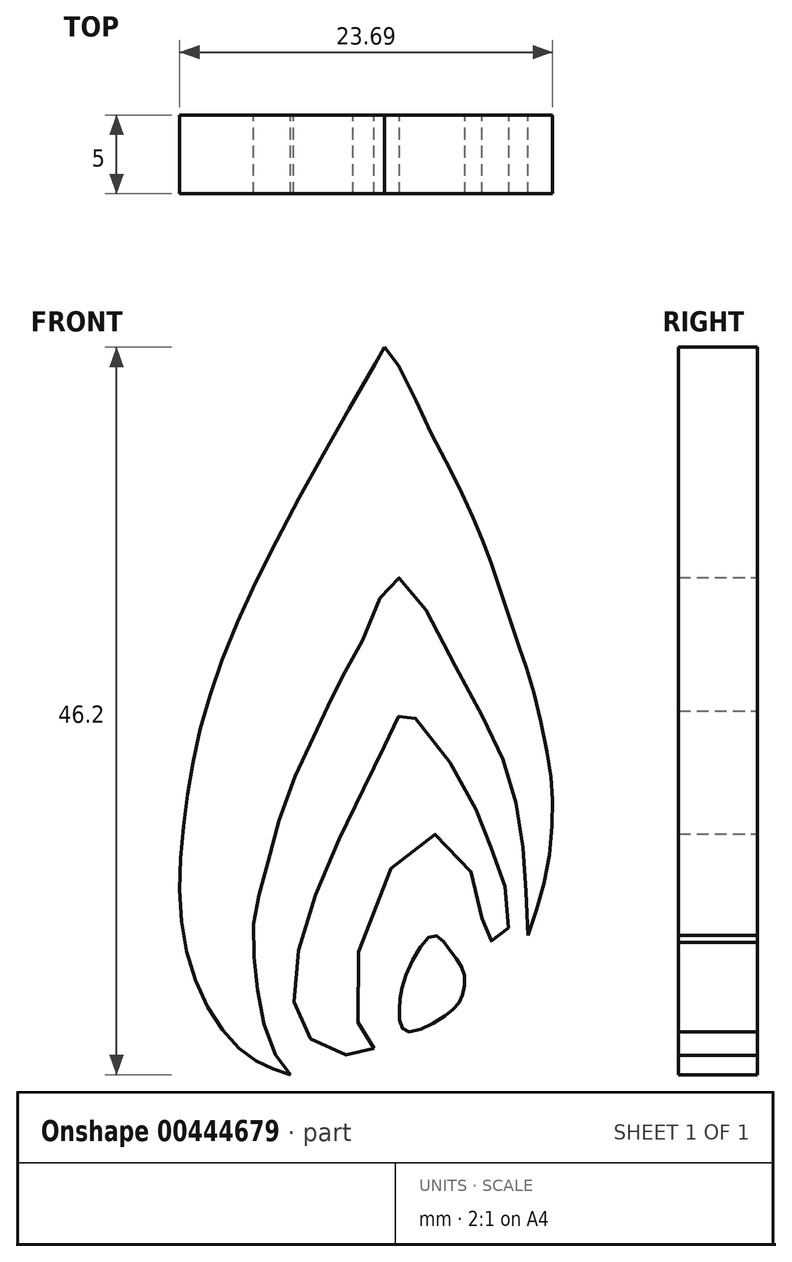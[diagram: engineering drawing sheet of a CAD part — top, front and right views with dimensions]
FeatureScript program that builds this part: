
annotation { "Feature Type Name" : "Feature", "Feature Type Description" : "" }
export const myFeature = defineFeature(function(context is Context, id is Id, definition is map)
    precondition{}
    {
        {
            var Q0;
            Q0=qCreatedBy(makeId("Front.planeOp"),FACE);
            var sketch = newSketch(context, id + "F0", { "sketchPlane" : qUnion([Q0])});
            skFitSpline(sketch, "E0", {"points": [v(-114.52, -36.4) * mm, v(-124.53, -55.47) * mm, v(-127.23, -66.27) * mm, v(-126.97, -75.26) * mm, v(-123.54, -81.14) * mm, v(-120.48, -82.6) * mm], "startDerivative": vector(-38.93, -67.33) * mm, "endDerivative": vector(25.9, -7.91) * mm});
            skFitSpline(sketch, "E1", {"points": [v(-105.42, -73.76) * mm, v(-104.24, -69.82) * mm, v(-103.84, -65.48) * mm, v(-104.14, -62.42) * mm, v(-105.23, -57.69) * mm, v(-106.21, -54.73) * mm, v(-107.79, -50) * mm, v(-108.97, -47.04) * mm, v(-110.55, -43.78) * mm, v(-111.74, -41.51) * mm, v(-114.52, -36.4) * mm, v(-115.13, -37.46) * mm], "startDerivative": vector(13.91, 39.07) * mm, "endDerivative": vector(-8.74, -32.14) * mm});
            skPoint(sketch, "E2.1.internal.orphan", {"position": v(-121.51, -80.47) * mm});
            skPoint(sketch, "E2.10.internal.orphan", {"position": v(-121.51, -70.21) * mm});
            skPoint(sketch, "E2.6.internal.orphan", {"position": v(-122.78, -75.26) * mm});
            skFitSpline(sketch, "E3", {"points": [v(-120.48, -82.6) * mm, v(-121.51, -81.26) * mm, v(-122.4, -78.31) * mm, v(-122.78, -75.26) * mm, v(-122.78, -72.47) * mm, v(-122.16, -70.02) * mm, v(-120.87, -65.33) * mm, v(-118.76, -60.6) * mm, v(-117.57, -58.04) * mm, v(-115.48, -54.06) * mm, v(-113.74, -51.03) * mm, v(-109.93, -56.83) * mm, v(-106.75, -63.2) * mm, v(-105.7, -68.57) * mm, v(-105.42, -73.76) * mm], "startDerivative": vector(-23.65, 25.1) * mm, "endDerivative": vector(2.23, -63.6) * mm});
            skFitSpline(sketch, "E4", {"points": [v(-115.18, -80.94) * mm, v(-116.41, -78.67) * mm, v(-111.88, -67.34) * mm, v(-108.43, -71.46) * mm, v(-108.17, -73.76) * mm, v(-107.1, -74.14) * mm, v(-106.68, -71.67) * mm, v(-107.81, -68.01) * mm, v(-109.67, -63.9) * mm, v(-113.17, -59.52) * mm, v(-113.58, -59.77) * mm, v(-114.61, -61.94) * mm, v(-117.29, -67.4) * mm, v(-119.97, -74.7) * mm, v(-119.76, -79.65) * mm, v(-116.98, -81.35) * mm, v(-115.18, -80.94) * mm]});
            skFitSpline(sketch, "E5", {"points": [v(-110.7, -78.88) * mm, v(-109.66, -77.8) * mm, v(-109.45, -76.2) * mm, v(-110.28, -74.81) * mm, v(-111.41, -73.76) * mm, v(-113.17, -76.36) * mm, v(-113.58, -78.62) * mm, v(-113.17, -79.86) * mm, v(-110.7, -78.88) * mm]});
            skSolve(sketch);
        }
        {
            var Q0;
            {var subQ4=sQuery(id+"F0.wireOp",EDGE,"E3");Q0=makeQuery(id+"F0.imprint","IMPRINT",FACE,{"disambiguationData":[TD([[makeQuery(id+"F0.imprint","IMPRINT",EDGE,{"derivedFrom":subQ4}),1.0]])]});}
            var Q1;
            Q1=makeQuery(id+"F0.imprint","IMPRINT",FACE,{"disambiguationData":[TD([[makeQuery(id+"F0.imprint","IMPRINT",EDGE,{"derivedFrom":sQuery(id+"F0.wireOp",EDGE,"E4")}),1.0]])]});
            var Q2;
            Q2=makeQuery(id+"F0.imprint","IMPRINT",FACE,{"disambiguationData":[TD([[makeQuery(id+"F0.imprint","IMPRINT",EDGE,{"derivedFrom":sQuery(id+"F0.wireOp",EDGE,"E5")}),1.0]])]});
            extrude(context, id + "F1", {"entities" : qUnion([Q0, Q1, Q2]), "depth" : 5 * mm});
        }
    });
